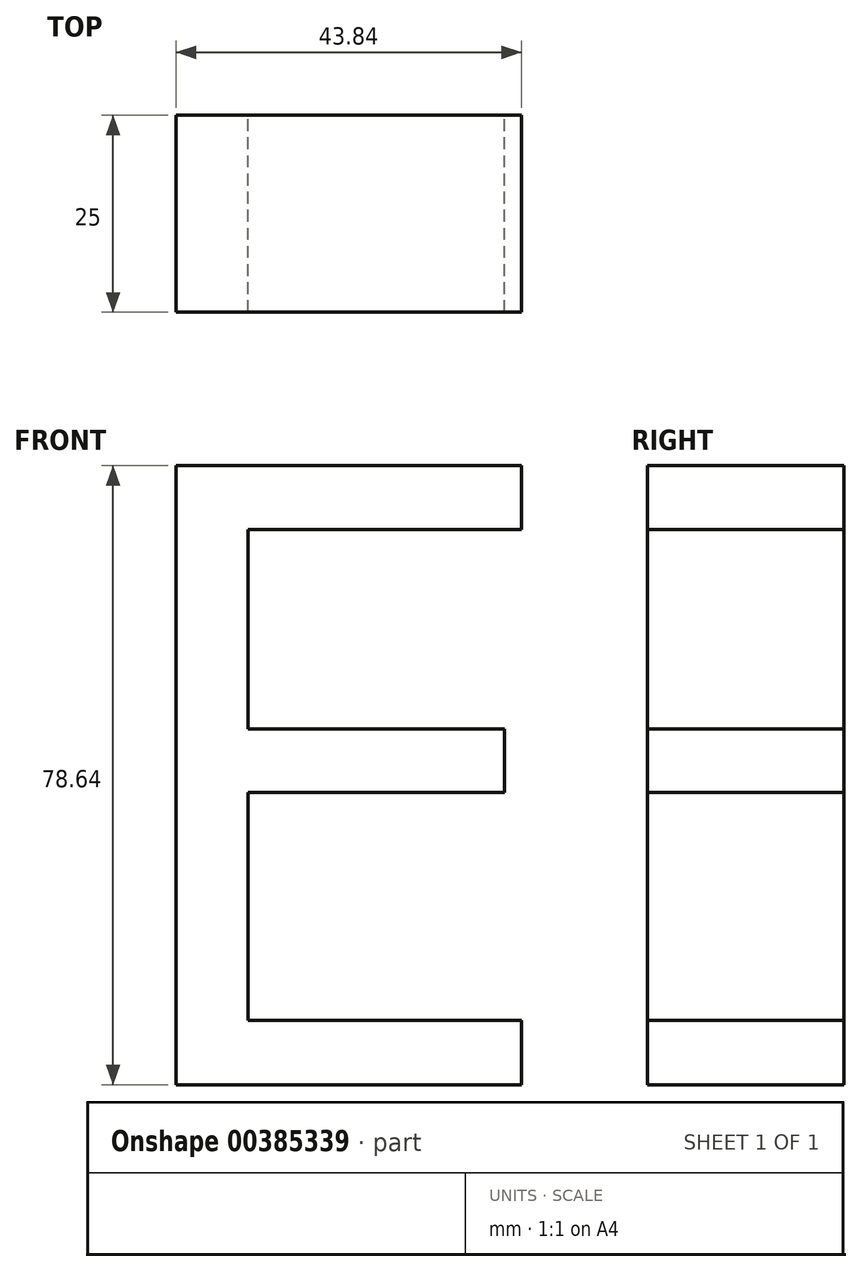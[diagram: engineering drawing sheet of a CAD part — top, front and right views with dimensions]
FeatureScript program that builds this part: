
annotation { "Feature Type Name" : "Feature", "Feature Type Description" : "" }
export const myFeature = defineFeature(function(context is Context, id is Id, definition is map)
    precondition{}
    {
        {
            var Q0;
            Q0=qCreatedBy(makeId("Front.planeOp"),FACE);
            var sketch = newSketch(context, id + "F0", { "sketchPlane" : qUnion([Q0])});
            skText(sketch, "E0", { "text": "E", "fontName": "OpenSans-Regular.ttf"});
            const initialGuessF0  = {"E0": [-0.05683, -0.0357, 1, 0, 0.07931]};
            skSetInitialGuess(sketch, initialGuessF0);
            skSolve(sketch);
        }
        {
            var Q0;
            Q0=qSketchRegion(id+"F0",true);
            extrude(context, id + "F1", {"entities" : qUnion([Q0]), "depth" : 25 * mm});
        }
    });
